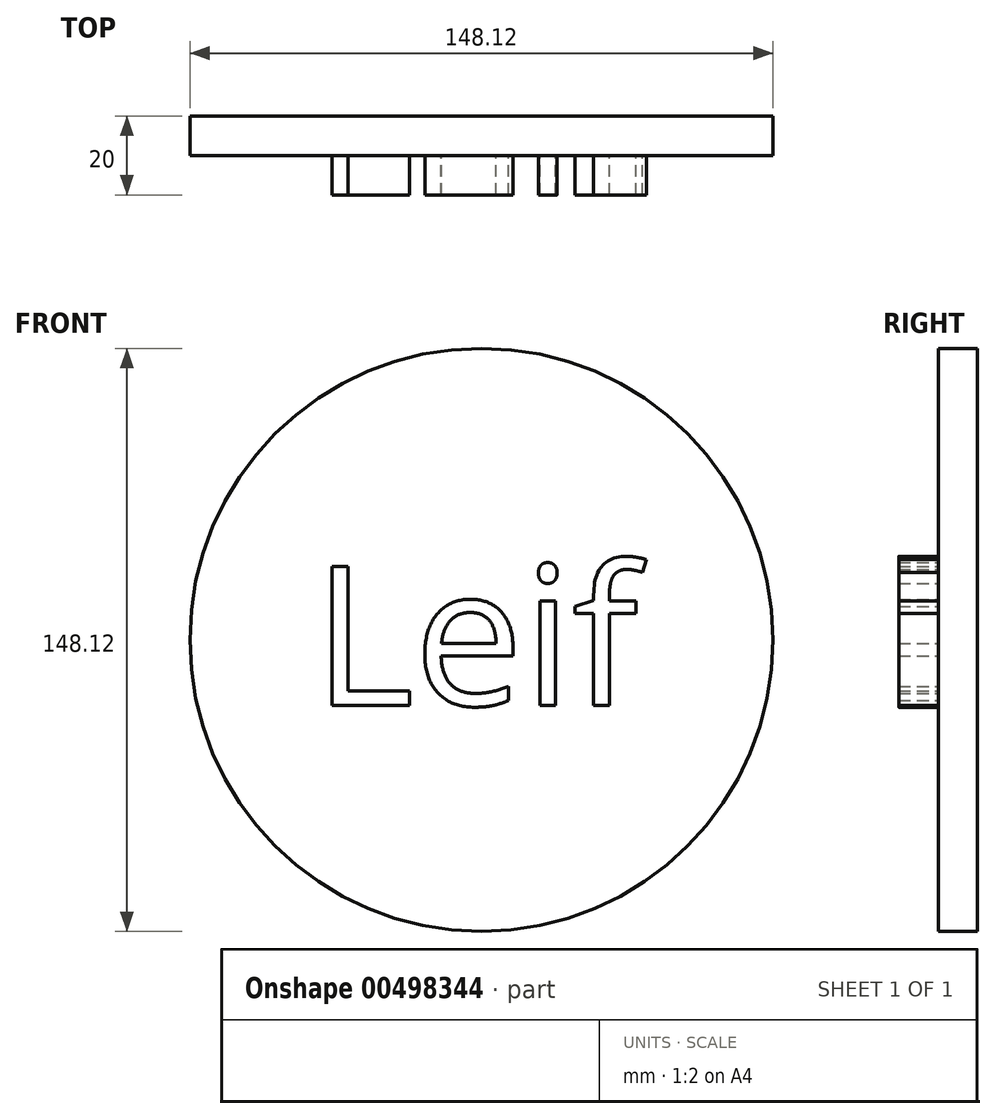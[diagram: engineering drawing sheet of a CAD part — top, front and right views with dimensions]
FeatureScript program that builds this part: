
annotation { "Feature Type Name" : "Feature", "Feature Type Description" : "" }
export const myFeature = defineFeature(function(context is Context, id is Id, definition is map)
    precondition{}
    {
        {
            var Q0;
            Q0=qCreatedBy(makeId("Front.planeOp"),FACE);
            var sketch = newSketch(context, id + "F0", { "sketchPlane" : qUnion([Q0])});
            skCircle(sketch, "E0", {"center": v(0, 0) * mm, "radius": 74.06 * mm});
            skSolve(sketch);
        }
        {
            var Q0;
            Q0=makeQuery(id+"F0.imprint","IMPRINT",FACE,{"disambiguationData":[TD([[makeQuery(id+"F0.imprint","IMPRINT",EDGE,{"derivedFrom":sQuery(id+"F0.wireOp",EDGE,"E0")}),1.0]])]});
            extrude(context, id + "F1", {"entities" : qUnion([Q0]), "depth" : 10 * mm});
        }
        {
            var Q0;
            Q0=makeQuery(id+"F1.opExtrude","CAP_FACE",FACE,{"disambiguationData":[OSD([sQuery(id+"F0.wireOp",EDGE,"E0")])],"isStart":false});
            var sketch = newSketch(context, id + "F2", { "sketchPlane" : qUnion([Q0])});
            skText(sketch, "E1", { "text": "Leif", "fontName": "OpenSans-Regular.ttf"});
            const initialGuessF2  = {"E1": [-0.04282, -0.01663, 1, 0, 0.0356]};
            skSetInitialGuess(sketch, initialGuessF2);
            skSolve(sketch);
        }
        {
            var Q0;
            Q0 = qSketchRegion(id + "F2", true);
            extrude(context, id + "F3", {"entities" : qUnion([Q0]), "operationType" : NewBodyOperationType.ADD, "depth" : 10 * mm});
        }
    });
